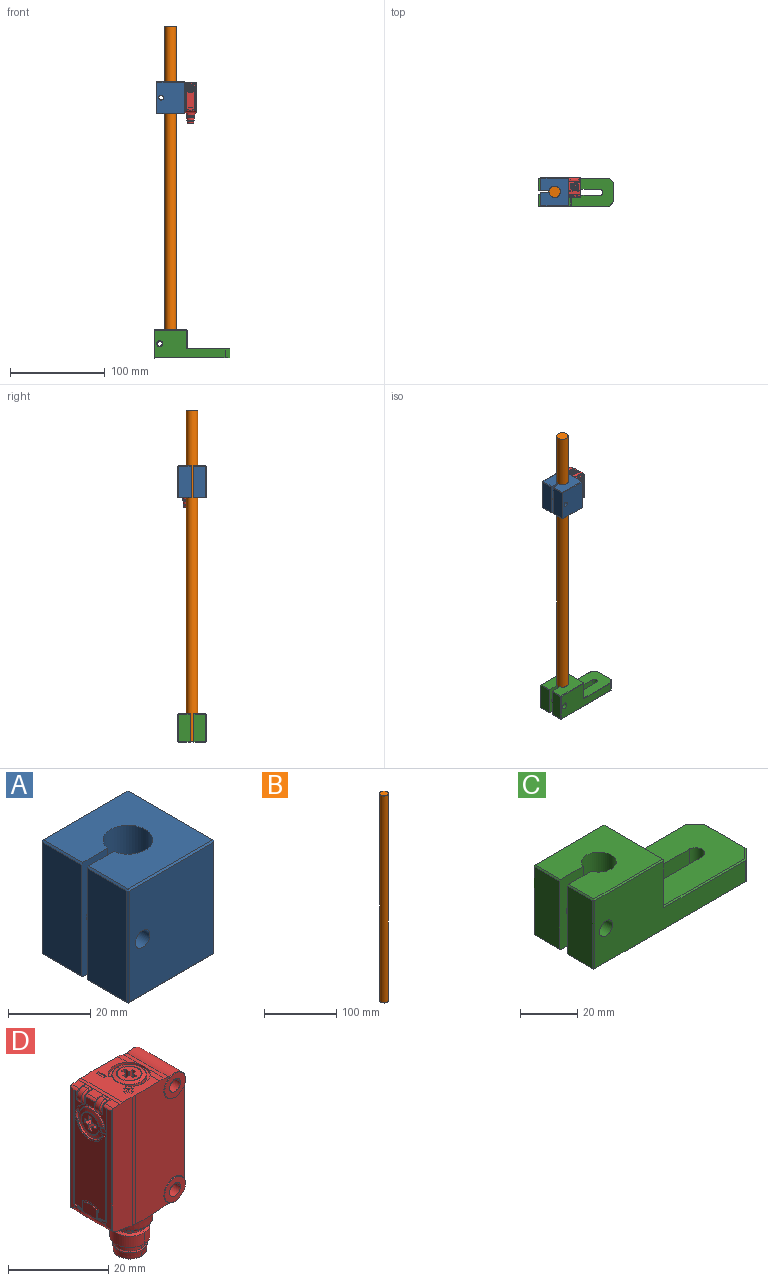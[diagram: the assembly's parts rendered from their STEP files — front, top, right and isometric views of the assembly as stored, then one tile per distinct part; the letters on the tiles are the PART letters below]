
ASSEMBLY  parts=4 mates=3
PART A: 38 faces, bbox 30x30x34 mm
  f0: plane 33x13.5mm, normal (-1,0,0), area 445.5mm2, adj f8,f28,f34,f37
  f1: plane 29x29mm, normal (0,0,1), area 709.1mm2, adj f3,f8,f9,f16,f18,f23,f28,f29
  f2: plane 29x29mm, normal (0,0,-1), area 709.1mm2, adj f3,f8,f9,f20,f25,f31,f35,f37
  f3: cylinder r=6.05mm len=34mm, axis (0,0,1), area 1224.1mm2, adj f1,f2,f8,f9
  f4: plane 33x29mm, normal (1,0,0), area 947.2mm2, adj f11,f13,f23,f24,f30,f31
  f5: plane 33x29mm, normal (0,1,0), area 924.8mm2, adj f15,f18,f19,f24,f25
  f6: plane 33x13.5mm, normal (-1,0,0), area 445.5mm2, adj f9,f16,f19,f20
  f7: plane 33x29mm, normal (0,-1,0), area 937.4mm2, adj f14,f29,f30,f34,f35
  f8: plane 34x9.03mm, normal (0,1,0), area 287.2mm2, adj f0,f1,f2,f3,f14,f28,f37
  f9: plane 34x9.03mm, normal (0,-1,0), area 274.7mm2, adj f1,f2,f3,f6,f15,f16,f20
  f10: cone r=0mm half-angle=59deg, axis (1,0,0), area 5.7mm2, adj f11
  f11: cylinder r=1.25mm len=13.5mm, axis (1,0,0), area 106mm2, adj f4,f10
  f12: cone r=0mm half-angle=59deg, axis (1,0,0), area 5.7mm2, adj f13
  f13: cylinder r=1.25mm len=13.5mm, axis (1,0,0), area 106mm2, adj f4,f12
  f14: cylinder r=2.5mm len=14mm, axis (0,1,0), area 219.9mm2, adj f7,f8
  f15: cylinder r=3.2mm len=14mm, axis (0,-1,0), area 281.5mm2, adj f5,f9
  f16: plane 13.5x0.5mm, normal (-0.71,0,0.71), area 9.5mm2, adj f1,f6,f9,f17
  f17: plane 0.5x0.5mm, normal (-0.58,0.58,0.58), area 0.2mm2, adj f16,f18,f19
  f18: plane 29x0.5mm, normal (0,0.71,0.71), area 20.5mm2, adj f1,f5,f17,f21
  f19: plane 33x0.5mm, normal (-0.71,0.71,0), area 23.3mm2, adj f5,f6,f17,f22
  f20: plane 13.5x0.5mm, normal (-0.71,0,-0.71), area 9.5mm2, adj f2,f6,f9,f22
  f21: plane 0.5x0.5mm, normal (0.58,0.58,0.58), area 0.2mm2, adj f18,f23,f24
  f22: plane 0.5x0.5mm, normal (-0.58,0.58,-0.58), area 0.2mm2, adj f19,f20,f25
  f23: plane 29x0.5mm, normal (0.71,0,0.71), area 20.5mm2, adj f1,f4,f21,f26
  f24: plane 33x0.5mm, normal (0.71,0.71,0), area 23.3mm2, adj f4,f5,f21,f27
  f25: plane 29x0.5mm, normal (0,0.71,-0.71), area 20.5mm2, adj f2,f5,f22,f27
  f26: plane 0.5x0.5mm, normal (0.58,-0.58,0.58), area 0.2mm2, adj f23,f29,f30
  f27: plane 0.5x0.5mm, normal (0.58,0.58,-0.58), area 0.2mm2, adj f24,f25,f31
  f28: plane 13.5x0.5mm, normal (-0.71,0,0.71), area 9.5mm2, adj f0,f1,f8,f32
  f29: plane 29x0.5mm, normal (0,-0.71,0.71), area 20.5mm2, adj f1,f7,f26,f32
  f30: plane 33x0.5mm, normal (0.71,-0.71,0), area 23.3mm2, adj f4,f7,f26,f33
  f31: plane 29x0.5mm, normal (0.71,0,-0.71), area 20.5mm2, adj f2,f4,f27,f33
  f32: plane 0.5x0.5mm, normal (-0.58,-0.58,0.58), area 0.2mm2, adj f28,f29,f34
  f33: plane 0.5x0.5mm, normal (0.58,-0.58,-0.58), area 0.2mm2, adj f30,f31,f35
  f34: plane 33x0.5mm, normal (-0.71,-0.71,0), area 23.3mm2, adj f0,f7,f32,f36
  f35: plane 29x0.5mm, normal (0,-0.71,-0.71), area 20.5mm2, adj f2,f7,f33,f36
  f36: plane 0.5x0.5mm, normal (-0.58,-0.58,-0.58), area 0.2mm2, adj f34,f35,f37
  f37: plane 13.5x0.5mm, normal (-0.71,0,-0.71), area 9.5mm2, adj f0,f2,f8,f36
PART B: 3 faces, bbox 12x12x350 mm
  f0: cylinder r=6mm len=350mm, axis (0,0,-1), area 13194.7mm2, adj f1,f2
  f1: plane 12x12mm, normal (0,0,1), area 113.1mm2, adj f0
  f2: plane 12x12mm, normal (0,0,-1), area 113.1mm2, adj f0
PART C: 53 faces, bbox 80x30x30 mm
  f0: plane 29x12.5mm, normal (-1,0,0), area 362.5mm2, adj f10,f41,f47,f50
  f1: plane 79x29mm, normal (0,0,-1), area 1949.4mm2, adj f2,f10,f11,f14,f15,f16,f17,f20
  f2: cylinder r=6.05mm len=30mm, axis (0,0,1), area 1018.1mm2, adj f1,f3,f10,f11
  f3: plane 34x29mm, normal (0,0,1), area 826.8mm2, adj f2,f10,f11,f18,f25,f32,f41,f42
  f4: plane 29x12.5mm, normal (-1,0,0), area 362.5mm2, adj f11,f18,f19,f20
  f5: plane 19.79x9mm, normal (1,0,0), area 178.1mm2, adj f12,f27,f36,f37
  f6: plane 44.5x29mm, normal (0,0,1), area 1108.2mm2, adj f7,f14,f15,f16,f17,f22,f23,f27
  f7: plane 29x19.5mm, normal (1,0,0), area 565.5mm2, adj f6,f26,f32,f33
  f8: plane 74.29x29mm, normal (0,-1,0), area 1316.5mm2, adj f33,f34,f42,f43,f47,f48,f51
  f9: plane 74.5x29mm, normal (0,1,0), area 1330.9mm2, adj f12,f19,f22,f25,f26,f28,f52
  f10: plane 30x11.79mm, normal (0,1,0), area 321.3mm2, adj f0,f1,f2,f3,f41,f50,f51
  f11: plane 30x11.79mm, normal (0,-1,0), area 333.8mm2, adj f1,f2,f3,f4,f18,f20,f52
  f12: plane 9x5mm, normal (0.71,0.71,0), area 63.6mm2, adj f5,f9,f23,f31
  f13: plane 9x4.71mm, normal (0.71,-0.71,0), area 59.9mm2, adj f35,f36,f43,f44
  f14: cylinder r=3.2mm len=10mm, axis (0,0,1), area 100.5mm2, adj f1,f6,f15,f17
  f15: plane 20x10mm, normal (0,1,0), area 200mm2, adj f1,f6,f14,f16
  f16: cylinder r=3.2mm len=10mm, axis (0,0,1), area 100.5mm2, adj f1,f6,f15,f17
  f17: plane 20x10mm, normal (0,-1,0), area 200mm2, adj f1,f6,f14,f16
  f18: plane 12.5x0.5mm, normal (-0.71,0,0.71), area 8.8mm2, adj f3,f4,f11,f21
  f19: plane 29x0.5mm, normal (-0.71,0.71,0), area 20.5mm2, adj f4,f9,f21,f24
  f20: plane 12.5x0.5mm, normal (-0.71,0,-0.71), area 8.8mm2, adj f1,f4,f11,f24
  f21: plane 0.5x0.5mm, normal (-0.58,0.58,0.58), area 0.2mm2, adj f18,f19,f25
  f22: plane 40.5x0.5mm, normal (0,0.71,0.71), area 28.4mm2, adj f6,f9,f23,f26
  f23: plane 5.21x5.21mm, normal (0.5,0.5,0.71), area 4.9mm2, adj f6,f12,f22,f27
  f24: plane 0.5x0.5mm, normal (-0.58,0.58,-0.58), area 0.2mm2, adj f19,f20,f28
  f25: plane 34x0.5mm, normal (0,0.71,0.71), area 24mm2, adj f3,f9,f21,f29
  f26: plane 20x0.5mm, normal (0.71,0.71,0), area 14mm2, adj f7,f9,f22,f29
  f27: plane 19.79x0.5mm, normal (0.71,0,0.71), area 13.9mm2, adj f5,f6,f23,f30
  f28: plane 74.5x0.5mm, normal (0,0.71,-0.71), area 52.6mm2, adj f1,f9,f24,f31
  f29: plane 0.5x0.5mm, normal (0.58,0.58,0.58), area 0.2mm2, adj f25,f26,f32
  f30: plane 0.5x0.5mm, normal (0.68,-0.28,0.68), area 0.1mm2, adj f27,f35,f36
  f31: plane 5.21x5.21mm, normal (0.5,0.5,-0.71), area 4.9mm2, adj f1,f12,f28,f37
  f32: plane 29x0.5mm, normal (0.71,0,0.71), area 20.5mm2, adj f3,f7,f29,f38
  f33: plane 20x0.5mm, normal (0.71,-0.71,0), area 14mm2, adj f7,f8,f34,f38
  f34: plane 40.29x0.5mm, normal (0,-0.71,0.71), area 28.3mm2, adj f6,f8,f33,f39
  f35: plane 5.06x5.06mm, normal (0.5,-0.5,0.71), area 4.7mm2, adj f6,f13,f30,f39
  f36: plane 9x0.35mm, normal (0.92,-0.38,0), area 3.4mm2, adj f5,f13,f30,f40
  f37: plane 19.79x0.5mm, normal (0.71,0,-0.71), area 13.9mm2, adj f1,f5,f31,f40
  f38: plane 0.5x0.5mm, normal (0.58,-0.58,0.58), area 0.2mm2, adj f32,f33,f42
  f39: plane 0.5x0.5mm, normal (0.28,-0.68,0.68), area 0.1mm2, adj f34,f35,f43
  f40: plane 0.5x0.5mm, normal (0.68,-0.28,-0.68), area 0.1mm2, adj f36,f37,f44
  f41: plane 12.5x0.5mm, normal (-0.71,0,0.71), area 8.8mm2, adj f0,f3,f10,f45
  f42: plane 34x0.5mm, normal (0,-0.71,0.71), area 24mm2, adj f3,f8,f38,f45
  f43: plane 9x0.35mm, normal (0.38,-0.92,0), area 3.4mm2, adj f8,f13,f39,f46
  f44: plane 5.06x5.06mm, normal (0.5,-0.5,-0.71), area 4.7mm2, adj f1,f13,f40,f46
  f45: plane 0.5x0.5mm, normal (-0.58,-0.58,0.58), area 0.2mm2, adj f41,f42,f47
  f46: plane 0.5x0.5mm, normal (0.28,-0.68,-0.68), area 0.1mm2, adj f43,f44,f48
  f47: plane 29x0.5mm, normal (-0.71,-0.71,0), area 20.5mm2, adj f0,f8,f45,f49
  f48: plane 74.29x0.5mm, normal (0,-0.71,-0.71), area 52.5mm2, adj f1,f8,f46,f49
  f49: plane 0.5x0.5mm, normal (-0.58,-0.58,-0.58), area 0.2mm2, adj f47,f48,f50
  f50: plane 12.5x0.5mm, normal (-0.71,0,-0.71), area 8.8mm2, adj f0,f1,f10,f49
  f51: cylinder r=3.2mm len=13mm, axis (0,1,0), area 261.4mm2, adj f8,f10
  f52: cylinder r=2.5mm len=13mm, axis (0,-1,0), area 204.2mm2, adj f9,f11
PART D: 278 faces, bbox 22.2x12.4x43.9 mm
  f0: cylinder r=4.2mm len=8.4mm, axis (0,0,1), area 9.5mm2, adj f1,f3,f4,f21,f22,f23,f24
  f1: plane 8.4x7.8mm, normal (0,0,1), area 14.2mm2, adj f0,f2,f3,f18,f19,f20,f21,f244
  f2: plane 0.6x0.32mm, normal (0.71,0.71,0), area 0.3mm2, adj f1,f3,f4,f18
  f3: cylinder r=4.2mm len=3.42mm, axis (0,0,1), area 2.4mm2, adj f0,f1,f2,f4
  f4: plane 12x10.39mm, normal (0,0,1), area 73.7mm2, adj f0,f2,f3,f5,f6,f7,f8,f9
  f5: plane 0.75x0.3mm, normal (0,1,0), area 0.2mm2, adj f4,f6,f16,f17
  f6: plane 0.7x0.3mm, normal (1,0,0), area 0.2mm2, adj f4,f5,f7,f17
  f7: plane 0.75x0.3mm, normal (0,-1,0), area 0.2mm2, adj f4,f6,f8,f17
  f8: plane 0.75x0.3mm, normal (1,0,0), area 0.2mm2, adj f4,f7,f9,f17
  f9: plane 0.7x0.3mm, normal (0,-1,0), area 0.2mm2, adj f4,f8,f10,f17
  f10: plane 0.75x0.3mm, normal (-1,0,0), area 0.2mm2, adj f4,f9,f11,f17
  f11: plane 0.75x0.3mm, normal (0,-1,0), area 0.2mm2, adj f4,f10,f12,f17
  f12: plane 0.7x0.3mm, normal (-1,0,0), area 0.2mm2, adj f4,f11,f13,f17
  f13: plane 0.75x0.3mm, normal (0,1,0), area 0.2mm2, adj f4,f12,f14,f17
  f14: plane 0.75x0.3mm, normal (-1,0,0), area 0.2mm2, adj f4,f13,f15,f17
  f15: plane 0.7x0.3mm, normal (0,1,0), area 0.2mm2, adj f4,f14,f16,f17
  f16: plane 0.75x0.3mm, normal (1,0,0), area 0.2mm2, adj f4,f5,f15,f17
  f17: plane 2.2x2.2mm, normal (0,0,1), area 2.6mm2, adj f5,f6,f7,f8,f9,f10,f11,f12
  f18: cylinder r=0.2mm len=0.6mm, axis (0,0,1), area 0.2mm2, adj f1,f2,f4,f19
  f19: cylinder r=3.6mm len=3.74mm, axis (0,0,1), area 2.4mm2, adj f1,f4,f18,f20
  f20: cylinder r=0.2mm len=0.6mm, axis (0,0,1), area 0.2mm2, adj f1,f4,f19,f21
  f21: plane 0.6x0.32mm, normal (0.71,-0.71,0), area 0.3mm2, adj f0,f1,f4,f20
  f22: cylinder r=5.84mm len=5.03mm, axis (0,-1,0), area 5.6mm2, adj f0,f4,f23,f62
  f23: plane 11.76x1.31mm, normal (0.25,0,0.97), area 15.1mm2, adj f0,f22,f24,f25,f62,f142
  f24: cylinder r=5.84mm len=5.03mm, axis (0,-1,0), area 5.6mm2, adj f0,f4,f23,f25
  f25: plane 31.53x13.98mm, normal (0.02,1,0), area 377.7mm2, adj f4,f23,f24,f26,f59,f63,f64,f78
  f26: plane 31.38x1mm, normal (0,1,0), area 31.3mm2, adj f4,f25,f27,f59
  f27: plane 31.29x0.05mm, normal (-1,0,0), area 1.6mm2, adj f4,f26,f28,f59
  f28: plane 31.3x5.44mm, normal (-0.02,1,0), area 166.9mm2, adj f4,f27,f29,f40,f41,f45,f56,f59
  f29: cylinder r=1mm len=2.36mm, axis (0,-1,0), area 1.8mm2, adj f28,f30,f39,f40,f55,f56,f57
  f30: plane 28.21x9.39mm, normal (-1,0,0), area 33.7mm2, adj f29,f31,f32,f34,f35,f38,f39,f43
  f31: plane 0.7x0.22mm, normal (0,-0.94,0.35), area 0.2mm2, adj f30,f32,f176,f227
  f32: cylinder r=4.2mm len=8.17mm, axis (1,0,0), area 7.9mm2, adj f30,f31,f33,f34,f166,f172,f176
  f33: plane 3.42x1.97mm, normal (-1,0,0), area 5.1mm2, adj f32,f34,f166,f167,f168,f169
  f34: torus R=1.4mm, axis (0,1,0), area 2.5mm2, adj f30,f32,f33,f35,f169,f170
  f35: cylinder r=1.8mm len=3.22mm, axis (0,-1,0), area 5.4mm2, adj f30,f34,f36,f38
  f36: plane 1.2x0.73mm, normal (0,0,1), area 0.9mm2, adj f35,f37,f170,f171
  f37: cylinder r=0.4mm len=0.88mm, axis (1,0,0), area 0.5mm2, adj f36,f38,f39,f171
  f38: torus R=1.4mm, axis (0,1,0), area 2.5mm2, adj f30,f35,f37,f39
  f39: plane 2.35x2.27mm, normal (0,1,0), area 0.9mm2, adj f29,f30,f37,f38,f40,f171
  f40: plane 11.78x1.75mm, normal (-0.14,0,0.99), area 15.2mm2, adj f28,f29,f39,f41,f42,f43,f159,f164
  f41: cylinder r=4.47mm len=11.81mm, axis (0,-1,0), area 9.3mm2, adj f4,f28,f40,f42
  f42: plane 31.3x5.44mm, normal (-0.02,-1,0), area 166.9mm2, adj f4,f40,f41,f43,f44,f45,f59,f60
  f43: cylinder r=1mm len=2.36mm, axis (0,-1,0), area 1.8mm2, adj f30,f40,f42,f44,f48,f58,f159
  f44: cylinder r=0.2mm len=29.58mm, axis (0,0,1), area 7.8mm2, adj f42,f43,f45,f48
  f45: torus R=76.35mm, axis (-1,0,0), area 29.6mm2, adj f28,f42,f44,f46,f47,f48,f54,f55
  f46: plane 8.39x2.75mm, normal (-1,0,0), area 11.3mm2, adj f45,f47,f49,f50,f51,f52,f53,f54
  f47: cylinder r=0.4mm len=0.64mm, axis (0,0,1), area 0mm2, adj f45,f46,f48,f49
  f48: plane 29.38x1.58mm, normal (-0.97,-0.22,0), area 32.9mm2, adj f43,f44,f45,f47,f49,f58
  f49: plane 2.65x0.47mm, normal (0,0.17,0.98), area 0.5mm2, adj f30,f46,f47,f48,f50,f58
  f50: plane 2.05x0.2mm, normal (0,-1,0), area 0.4mm2, adj f30,f46,f49,f51
  f51: cylinder r=3.7mm len=3.9mm, axis (1,0,0), area 0.8mm2, adj f30,f46,f50,f52
  f52: plane 2.05x0.2mm, normal (0,1,0), area 0.4mm2, adj f30,f46,f51,f53
  f53: plane 2.65x0.47mm, normal (0,-0.17,0.98), area 0.5mm2, adj f30,f46,f52,f54,f55,f57
  f54: cylinder r=0.4mm len=0.64mm, axis (0,0,1), area 0mm2, adj f45,f46,f53,f55
  f55: plane 29.38x1.58mm, normal (-0.97,0.22,0), area 32.9mm2, adj f29,f45,f53,f54,f56,f57
  f56: cylinder r=0.2mm len=29.58mm, axis (0,0,1), area 7.8mm2, adj f28,f29,f45,f55
  f57: plane 27.55x0.12mm, normal (0,-1,0), area 3.2mm2, adj f29,f30,f53,f55
  f58: plane 27.55x0.12mm, normal (0,1,0), area 3.2mm2, adj f30,f43,f48,f49
  f59: torus R=36.05mm, axis (-1,0,0), area 61.3mm2, adj f25,f26,f27,f28,f42,f45,f60,f61
  f60: plane 31.29x0.05mm, normal (-1,0,0), area 1.6mm2, adj f4,f42,f59,f61
  f61: plane 31.38x1mm, normal (0,-1,0), area 31.3mm2, adj f4,f59,f60,f62
  f62: plane 31.53x13.98mm, normal (0.02,-1,0), area 377.7mm2, adj f4,f22,f23,f59,f61,f63,f77,f78
  f63: cylinder r=2.2mm len=11.51mm, axis (0,-1,0), area 7.9mm2, adj f25,f62,f64,f66,f77,f141
  f64: cylinder r=0.1mm len=24.36mm, axis (0,0,1), area 3.7mm2, adj f25,f63,f65,f66,f78
  f65: torus R=75.79mm, axis (-1,0,0), area 1.6mm2, adj f64,f66,f77,f78
  f66: plane 23.72x11.31mm, normal (1,0,0), area 41.3mm2, adj f63,f64,f65,f67,f68,f69,f70,f77
  f67: plane 22.4x1.15mm, normal (0,1,0), area 25.8mm2, adj f66,f68,f70,f71
  f68: plane 10.1x1.15mm, normal (0,0,1), area 11.6mm2, adj f66,f67,f69,f71
  f69: plane 22.4x1.15mm, normal (0,-1,0), area 25.8mm2, adj f66,f68,f70,f71
  f70: plane 10.1x1.15mm, normal (0,0,-1), area 11.6mm2, adj f66,f67,f69,f71
  f71: plane 22.4x10.1mm, normal (1,0,0), area 6.5mm2, adj f67,f68,f69,f70,f72,f73,f74,f75
  f72: plane 9.9x1.1mm, normal (0,0,-1), area 10.9mm2, adj f71,f73,f75,f76
  f73: plane 22.2x1.1mm, normal (0,-1,0), area 24.4mm2, adj f71,f72,f74,f76
  f74: plane 9.9x1.1mm, normal (0,0,1), area 10.9mm2, adj f71,f73,f75,f76
  f75: plane 22.2x1.1mm, normal (0,1,0), area 24.4mm2, adj f71,f72,f74,f76
  f76: plane 22.2x9.9mm, normal (1,0,0), area 219.8mm2, adj f72,f73,f74,f75
  f77: cylinder r=0.1mm len=24.36mm, axis (0,0,1), area 3.7mm2, adj f62,f63,f65,f66,f78
  f78: cylinder r=3mm len=11.8mm, axis (0,-1,0), area 3.5mm2, adj f25,f62,f64,f65,f77,f79,f81,f95
  f79: cylinder r=3mm len=11.8mm, axis (0,-1,0), area 71.3mm2, adj f25,f62,f78,f80,f94,f96
  f80: torus R=2.9mm, axis (0,1,0), area 1.5mm2, adj f79,f81,f82
  f81: torus R=2.9mm, axis (0,1,0), area 1.5mm2, adj f78,f80,f82
  f82: plane 5.8x5.8mm, normal (0,1,0), area 19.1mm2, adj f80,f81,f83,f84
  f83: cylinder r=1.53mm len=3.06mm, axis (0,-1,0), area 9.6mm2, adj f82,f84,f86
  f84: cylinder r=1.53mm len=3.06mm, axis (0,-1,0), area 9.6mm2, adj f82,f83,f85
  f85: cone r=1.23mm half-angle=45deg, axis (0,1,0), area 1.8mm2, adj f84,f86,f88
  f86: cone r=1.23mm half-angle=45deg, axis (0,1,0), area 1.8mm2, adj f83,f85,f87
  f87: cylinder r=1.23mm len=7.4mm, axis (0,-1,0), area 28.6mm2, adj f86,f88,f90
  f88: cylinder r=1.23mm len=7.4mm, axis (0,-1,0), area 28.6mm2, adj f85,f87,f89
  f89: cone r=1.53mm half-angle=45deg, axis (0,-1,0), area 1.8mm2, adj f88,f90,f92
  f90: cone r=1.53mm half-angle=45deg, axis (0,-1,0), area 1.8mm2, adj f87,f89,f91
  f91: cylinder r=1.53mm len=3.06mm, axis (0,-1,0), area 9.6mm2, adj f90,f92,f93
  f92: cylinder r=1.53mm len=3.06mm, axis (0,-1,0), area 9.6mm2, adj f89,f91,f93
  f93: plane 5.8x5.8mm, normal (0,-1,0), area 19.1mm2, adj f91,f92,f94,f95
  f94: torus R=2.9mm, axis (0,1,0), area 1.5mm2, adj f79,f93,f95
  f95: torus R=2.9mm, axis (0,1,0), area 1.5mm2, adj f78,f93,f94
  f96: torus R=36.05mm, axis (-1,0,0), area 20.4mm2, adj f25,f62,f79,f97,f101
  f97: plane 12.3x8.55mm, normal (0,0,-1), area 21.1mm2, adj f25,f59,f62,f96,f98,f101
  f98: cone r=4.95mm half-angle=6deg, axis (0,0,1), area 50.9mm2, adj f97,f99,f100,f101
  f99: torus R=4mm, axis (0,0,-1), area 10.8mm2, adj f98,f100,f101,f102
  f100: torus R=4mm, axis (0,0,-1), area 10.8mm2, adj f98,f99,f101,f102
  f101: cone r=4.95mm half-angle=6deg, axis (0,0,1), area 50.9mm2, adj f96,f97,f98,f99,f100
  f102: plane 8.01x8.01mm, normal (0,0,-1), area 14mm2, adj f99,f100,f103,f104
  f103: cylinder r=3.4mm len=6.8mm, axis (0,0,1), area 10.7mm2, adj f102,f104,f106
  f104: cylinder r=3.4mm len=6.8mm, axis (0,0,1), area 10.7mm2, adj f102,f103,f105
  f105: cone r=3.4mm half-angle=60deg, axis (0,0,-1), area 8.1mm2, adj f104,f106,f108
  f106: cone r=3.4mm half-angle=60deg, axis (0,0,-1), area 8.1mm2, adj f103,f105,f107
  f107: cylinder r=4mm len=8mm, axis (0,0,1), area 34.2mm2, adj f106,f108,f110
  f108: cylinder r=4mm len=8mm, axis (0,0,1), area 34.2mm2, adj f105,f107,f109
  f109: cone r=4mm half-angle=60deg, axis (0,0,1), area 9.9mm2, adj f108,f110,f112
  f110: cone r=4mm half-angle=60deg, axis (0,0,1), area 9.9mm2, adj f107,f109,f111
  f111: cylinder r=3.25mm len=6.5mm, axis (0,0,1), area 10.2mm2, adj f110,f112,f114
  f112: cylinder r=3.25mm len=6.5mm, axis (0,0,1), area 10.2mm2, adj f109,f111,f113
  f113: cone r=3.25mm half-angle=38.7deg, axis (0,0,-1), area 2.9mm2, adj f112,f114,f116
  f114: cone r=3.25mm half-angle=38.7deg, axis (0,0,-1), area 2.9mm2, adj f111,f113,f115
  f115: torus R=3.35mm, axis (0,0,-1), area 0.9mm2, adj f114,f116,f118
  f116: torus R=3.35mm, axis (0,0,-1), area 0.9mm2, adj f113,f115,f117
  f117: cone r=3.45mm half-angle=6.5deg, axis (0,0,1), area 16.3mm2, adj f116,f118,f120
  f118: cone r=3.45mm half-angle=6.5deg, axis (0,0,1), area 16.3mm2, adj f115,f117,f119
  f119: torus R=3.07mm, axis (0,0,-1), area 2.9mm2, adj f118,f120,f121
  f120: torus R=3.07mm, axis (0,0,-1), area 2.9mm2, adj f117,f119,f121
  f121: plane 6.14x6.14mm, normal (0,0,-1), area 3.2mm2, adj f119,f120,f122,f123
  f122: cylinder r=2.9mm len=5.8mm, axis (0,0,1), area 45.6mm2, adj f121,f123,f124
  f123: cylinder r=2.9mm len=5.8mm, axis (0,0,1), area 45.6mm2, adj f121,f122,f124
  f124: plane 5.8x5.8mm, normal (0,0,-1), area 23.3mm2, adj f122,f123,f125,f126,f129,f130,f133,f134
  f125: cylinder r=0.5mm len=4.2mm, axis (0,0,1), area 6.6mm2, adj f124,f126,f128
  f126: cylinder r=0.5mm len=4.2mm, axis (0,0,1), area 6.6mm2, adj f124,f125,f127
  f127: sphere r=0.5mm, area 0.9mm2, adj f126,f128
  f128: sphere r=0.5mm, area 0.9mm2, adj f125,f127
  f129: cylinder r=0.5mm len=4.2mm, axis (0,0,1), area 6.6mm2, adj f124,f130,f132
  f130: cylinder r=0.5mm len=4.2mm, axis (0,0,1), area 6.6mm2, adj f124,f129,f131
  f131: sphere r=0.5mm, area 0.9mm2, adj f130,f132
  f132: sphere r=0.5mm, area 0.9mm2, adj f129,f131
  f133: cylinder r=0.5mm len=4.2mm, axis (0,0,1), area 6.6mm2, adj f124,f134,f136
  f134: cylinder r=0.5mm len=4.2mm, axis (0,0,1), area 6.6mm2, adj f124,f133,f135
  f135: sphere r=0.5mm, area 0.9mm2, adj f134,f136
  f136: sphere r=0.5mm, area 0.9mm2, adj f133,f135
  f137: cylinder r=0.5mm len=4.2mm, axis (0,0,1), area 6.6mm2, adj f124,f138,f140
  f138: cylinder r=0.5mm len=4.2mm, axis (0,0,1), area 6.6mm2, adj f124,f137,f139
  f139: sphere r=0.5mm, area 0.9mm2, adj f138,f140
  f140: sphere r=0.5mm, area 0.9mm2, adj f137,f139
  f141: cylinder r=3mm len=11.8mm, axis (0,-1,0), area 11.1mm2, adj f25,f62,f63,f142,f144,f157
  f142: cylinder r=3mm len=11.8mm, axis (0,-1,0), area 74.6mm2, adj f23,f25,f62,f141,f143,f158
  f143: torus R=2.9mm, axis (0,1,0), area 1.5mm2, adj f142,f144,f145
  f144: torus R=2.9mm, axis (0,1,0), area 1.5mm2, adj f141,f143,f145
  f145: plane 5.8x5.8mm, normal (0,-1,0), area 19.1mm2, adj f143,f144,f146,f147
  f146: cylinder r=1.53mm len=3.06mm, axis (0,-1,0), area 9.6mm2, adj f145,f147,f149
  f147: cylinder r=1.53mm len=3.06mm, axis (0,-1,0), area 9.6mm2, adj f145,f146,f148
  f148: cone r=1.53mm half-angle=45deg, axis (0,-1,0), area 1.8mm2, adj f147,f149,f151
  f149: cone r=1.53mm half-angle=45deg, axis (0,-1,0), area 1.8mm2, adj f146,f148,f150
  f150: cylinder r=1.23mm len=7.4mm, axis (0,-1,0), area 28.6mm2, adj f149,f151,f153
  f151: cylinder r=1.23mm len=7.4mm, axis (0,-1,0), area 28.6mm2, adj f148,f150,f152
  f152: cone r=1.23mm half-angle=45deg, axis (0,1,0), area 1.8mm2, adj f151,f153,f155
  f153: cone r=1.23mm half-angle=45deg, axis (0,1,0), area 1.8mm2, adj f150,f152,f154
  f154: cylinder r=1.53mm len=3.06mm, axis (0,-1,0), area 9.6mm2, adj f153,f155,f156
  f155: cylinder r=1.53mm len=3.06mm, axis (0,-1,0), area 9.6mm2, adj f152,f154,f156
  f156: plane 5.8x5.8mm, normal (0,1,0), area 19.1mm2, adj f154,f155,f157,f158
  f157: torus R=2.9mm, axis (0,1,0), area 1.5mm2, adj f141,f156,f158
  f158: torus R=2.9mm, axis (0,1,0), area 1.5mm2, adj f142,f156,f157
  f159: plane 2.35x2.27mm, normal (0,-1,0), area 0.9mm2, adj f30,f40,f43,f160,f163,f164
  f160: torus R=1.4mm, axis (0,1,0), area 2.5mm2, adj f30,f159,f161,f163
  f161: cylinder r=1.8mm len=3.22mm, axis (0,-1,0), area 5.4mm2, adj f30,f160,f162,f166
  f162: plane 1.2x0.73mm, normal (0,0,1), area 0.9mm2, adj f161,f163,f164,f165
  f163: cylinder r=0.4mm len=0.88mm, axis (1,0,0), area 0.5mm2, adj f159,f160,f162,f164
  f164: plane 2.06x0.66mm, normal (0.94,0,0.34), area 1.2mm2, adj f40,f159,f162,f163,f165,f167
  f165: cylinder r=0.4mm len=0.88mm, axis (1,0,0), area 0.5mm2, adj f162,f164,f166,f167
  f166: torus R=1.4mm, axis (0,1,0), area 2.5mm2, adj f30,f32,f33,f161,f165,f167
  f167: plane 2.35x2.27mm, normal (0,1,0), area 0.9mm2, adj f33,f40,f164,f165,f166,f168
  f168: cylinder r=1mm len=3mm, axis (0,-1,0), area 2.3mm2, adj f33,f40,f167,f169
  f169: plane 2.35x2.27mm, normal (0,-1,0), area 0.9mm2, adj f33,f34,f40,f168,f170,f171
  f170: cylinder r=0.4mm len=0.88mm, axis (1,0,0), area 0.5mm2, adj f34,f36,f169,f171
  f171: plane 2.06x0.66mm, normal (0.94,0,0.34), area 1.2mm2, adj f36,f37,f39,f40,f169,f170
  f172: plane 0.7x0.22mm, normal (0,0.94,0.35), area 0.2mm2, adj f30,f32,f173,f176
  f173: cylinder r=0.17mm len=0.7mm, axis (1,0,0), area 0.1mm2, adj f30,f172,f174,f176
  f174: plane 0.7x0.18mm, normal (0,0.77,-0.64), area 0.2mm2, adj f30,f173,f175,f176
  f175: cylinder r=4.2mm len=1.11mm, axis (1,0,0), area 0.8mm2, adj f30,f174,f176,f222
  f176: plane 8.4x7.85mm, normal (-1,0,0), area 10.2mm2, adj f31,f32,f172,f173,f174,f175,f177,f178
  f177: cone r=3.46mm half-angle=5deg, axis (1,0,0), area 5mm2, adj f176,f178,f181,f212
  f178: cone r=3.46mm half-angle=5deg, axis (1,0,0), area 5mm2, adj f176,f177,f179,f180
  f179: plane 1.59x0.82mm, normal (0,0,-1), area 0.4mm2, adj f176,f178,f180,f183,f184,f186,f213,f214
  f180: torus R=3.36mm, axis (1,0,0), area 1.2mm2, adj f178,f179,f181,f183
  f181: torus R=3.36mm, axis (1,0,0), area 1.2mm2, adj f177,f180,f182,f212
  f182: cone r=2.56mm half-angle=75deg, axis (1,0,0), area 7.5mm2, adj f181,f183,f185,f212
  f183: cone r=2.56mm half-angle=75deg, axis (1,0,0), area 7.5mm2, adj f179,f180,f182,f184
  f184: torus R=2.43mm, axis (1,0,0), area 1mm2, adj f179,f183,f185,f186
  f185: torus R=2.43mm, axis (1,0,0), area 1mm2, adj f182,f184,f186,f212
  f186: plane 5.47x4.87mm, normal (-1,0,0), area 13.7mm2, adj f179,f184,f185,f187,f188,f190,f191,f192
  f187: plane 1.9x0.75mm, normal (0,1,0), area 1.4mm2, adj f186,f188,f189,f211
  f188: cylinder r=0.1mm len=1.9mm, axis (1,0,0), area 0.3mm2, adj f186,f187,f189,f190
  f189: plane 3.4x3.4mm, normal (-1,0,0), area 5.6mm2, adj f187,f188,f190,f191,f192,f193,f194,f195
  f190: plane 1.9x0.93mm, normal (0,0,1), area 1.8mm2, adj f186,f188,f189,f191
  f191: cylinder r=0.2mm len=1.9mm, axis (1,0,0), area 0.6mm2, adj f186,f189,f190,f192
  f192: plane 1.9x0.93mm, normal (0,1,0), area 1.8mm2, adj f186,f189,f191,f193
  f193: cylinder r=0.1mm len=1.9mm, axis (1,0,0), area 0.3mm2, adj f186,f189,f192,f194
  f194: plane 1.9x0.75mm, normal (0,0,1), area 1.4mm2, adj f186,f189,f193,f195
  f195: cylinder r=0.1mm len=1.9mm, axis (1,0,0), area 0.3mm2, adj f186,f189,f194,f196
  f196: plane 1.9x0.93mm, normal (0,-1,0), area 1.8mm2, adj f186,f189,f195,f197
  f197: cylinder r=0.2mm len=1.9mm, axis (1,0,0), area 0.6mm2, adj f186,f189,f196,f198
  f198: plane 1.9x0.93mm, normal (0,0,1), area 1.8mm2, adj f186,f189,f197,f199
  f199: cylinder r=0.1mm len=1.9mm, axis (1,0,0), area 0.3mm2, adj f186,f189,f198,f200
  f200: plane 1.9x0.75mm, normal (0,-1,0), area 1.4mm2, adj f186,f189,f199,f201
  f201: cylinder r=0.1mm len=1.9mm, axis (1,0,0), area 0.3mm2, adj f186,f189,f200,f202
  f202: plane 1.9x0.93mm, normal (0,0,-1), area 1.8mm2, adj f186,f189,f201,f203
  f203: cylinder r=0.2mm len=1.9mm, axis (1,0,0), area 0.6mm2, adj f186,f189,f202,f204
  f204: plane 1.9x0.93mm, normal (0,-1,0), area 1.8mm2, adj f186,f189,f203,f205
  f205: cylinder r=0.1mm len=1.9mm, axis (1,0,0), area 0.3mm2, adj f186,f189,f204,f206
  f206: plane 1.9x0.75mm, normal (0,0,-1), area 1.4mm2, adj f186,f189,f205,f207
  f207: cylinder r=0.1mm len=1.9mm, axis (1,0,0), area 0.3mm2, adj f186,f189,f206,f208
  f208: plane 1.9x0.93mm, normal (0,1,0), area 1.8mm2, adj f186,f189,f207,f209
  f209: cylinder r=0.2mm len=1.9mm, axis (1,0,0), area 0.6mm2, adj f186,f189,f208,f210
  f210: plane 1.9x0.93mm, normal (0,0,-1), area 1.8mm2, adj f186,f189,f209,f211
  f211: cylinder r=0.1mm len=1.9mm, axis (1,0,0), area 0.3mm2, adj f186,f187,f189,f210
  f212: plane 1.59x0.82mm, normal (0,0,1), area 0.4mm2, adj f176,f177,f181,f182,f185,f186,f213,f214
  f213: cylinder r=0.5mm len=1.09mm, axis (0,0,1), area 0.1mm2, adj f179,f186,f212,f214
  f214: plane 1.09x0.92mm, normal (-0.97,-0.26,0), area 1mm2, adj f179,f212,f213,f215,f216,f217,f218,f219
  f215: plane 0.58x0.14mm, normal (0,-0.62,0.79), area 0.1mm2, adj f176,f212,f214,f216
  f216: cylinder r=4.1mm len=0.54mm, axis (1,0,0), area 0mm2, adj f176,f214,f215,f217
  f217: plane 0.81x0.54mm, normal (0,-1,0), area 0.4mm2, adj f176,f214,f216,f218
  f218: cylinder r=4.1mm len=0.54mm, axis (1,0,0), area 0mm2, adj f176,f214,f217,f219
  f219: plane 0.58x0.14mm, normal (0,-0.62,-0.79), area 0.1mm2, adj f176,f179,f214,f218
  f220: cylinder r=3.65mm len=7.13mm, axis (1,0,0), area 6.9mm2, adj f30,f176,f221,f223
  f221: cylinder r=0.1mm len=0.7mm, axis (1,0,0), area 0.1mm2, adj f30,f176,f220,f222
  f222: plane 0.7x0.48mm, normal (0,0,1), area 0.3mm2, adj f30,f175,f176,f221
  f223: cylinder r=0.1mm len=0.7mm, axis (1,0,0), area 0.1mm2, adj f30,f176,f220,f224
  f224: plane 0.7x0.48mm, normal (0,0,1), area 0.3mm2, adj f30,f176,f223,f225
  f225: cylinder r=4.2mm len=1.11mm, axis (1,0,0), area 0.8mm2, adj f30,f176,f224,f226
  f226: plane 0.7x0.18mm, normal (0,-0.77,-0.64), area 0.2mm2, adj f30,f176,f225,f227
  f227: cylinder r=0.17mm len=0.7mm, axis (1,0,0), area 0.1mm2, adj f30,f31,f176,f226
  f228: cylinder r=3.95mm len=7.53mm, axis (-1,0,0), area 1mm2, adj f30,f229,f236,f238
  f229: plane 20.67x8.6mm, normal (-1,0,0), area 150.9mm2, adj f228,f230,f231,f232,f233,f234,f235,f236
  f230: cylinder r=19.7mm len=2.05mm, axis (-1,0,0), area 0.2mm2, adj f30,f229,f231,f237
  f231: plane 1.98x0.1mm, normal (0,1,0), area 0.2mm2, adj f30,f229,f230,f232
  f232: cylinder r=4mm len=4.5mm, axis (-1,0,0), area 0.5mm2, adj f30,f229,f231,f233
  f233: plane 1.98x0.1mm, normal (0,-1,0), area 0.2mm2, adj f30,f229,f232,f234
  f234: cylinder r=19.7mm len=2.05mm, axis (-1,0,0), area 0.2mm2, adj f30,f229,f233,f235
  f235: plane 20.32x0.1mm, normal (0,1,0), area 2mm2, adj f30,f229,f234,f236
  f236: plane 0.54x0.1mm, normal (0,0,1), area 0.1mm2, adj f30,f228,f229,f235
  f237: plane 20.32x0.1mm, normal (0,-1,0), area 2mm2, adj f30,f229,f230,f238
  f238: plane 0.54x0.1mm, normal (0,0,1), area 0.1mm2, adj f30,f228,f229,f237
  f239: plane 2.2x0.3mm, normal (1,0,0), area 0.7mm2, adj f4,f240,f242,f243
  f240: plane 0.7x0.3mm, normal (0,-1,0), area 0.2mm2, adj f4,f239,f241,f243
  f241: plane 2.2x0.3mm, normal (-1,0,0), area 0.7mm2, adj f4,f240,f242,f243
  f242: plane 0.7x0.3mm, normal (0,1,0), area 0.2mm2, adj f4,f239,f241,f243
  f243: plane 2.2x0.7mm, normal (0,0,1), area 1.5mm2, adj f239,f240,f241,f242
  f244: cone r=3.45mm half-angle=5deg, axis (0,0,-1), area 5.2mm2, adj f1,f245,f247
  f245: cone r=3.45mm half-angle=5deg, axis (0,0,-1), area 5.2mm2, adj f1,f244,f246
  f246: torus R=3.35mm, axis (0,0,-1), area 1.3mm2, adj f245,f247,f249
  f247: torus R=3.35mm, axis (0,0,-1), area 1.3mm2, adj f244,f246,f248
  f248: cone r=2.56mm half-angle=75deg, axis (0,0,-1), area 7.9mm2, adj f247,f249,f251
  f249: cone r=2.56mm half-angle=75deg, axis (0,0,-1), area 7.9mm2, adj f246,f248,f250
  f250: torus R=2.43mm, axis (0,0,-1), area 1mm2, adj f249,f251,f252
  f251: torus R=2.43mm, axis (0,0,-1), area 1mm2, adj f248,f250,f252
  f252: plane 4.87x4.87mm, normal (0,0,1), area 13.6mm2, adj f250,f251,f253,f254,f255,f257,f258,f259
  f253: cylinder r=0.2mm len=2mm, axis (0,0,-1), area 0.6mm2, adj f252,f254,f256,f277
  f254: plane 2x0.61mm, normal (0,1,0), area 1.2mm2, adj f252,f253,f255,f256
  f255: cylinder r=0.1mm len=2mm, axis (0,0,-1), area 0.3mm2, adj f252,f254,f256,f258
  f256: plane 3.4x2.77mm, normal (0,0,1), area 5mm2, adj f253,f254,f255,f257,f258,f259,f260,f261
  f257: cylinder r=0.1mm len=2mm, axis (0,0,-1), area 0.3mm2, adj f252,f256,f258,f259
  f258: plane 2x0.75mm, normal (1,0,0), area 1.5mm2, adj f252,f255,f256,f257
  f259: plane 2x0.61mm, normal (0,-1,0), area 1.2mm2, adj f252,f256,f257,f260
  f260: cylinder r=0.2mm len=2mm, axis (0,0,-1), area 0.6mm2, adj f252,f256,f259,f261
  f261: plane 2x0.93mm, normal (1,0,0), area 1.8mm2, adj f252,f256,f260,f262
  f262: cylinder r=0.1mm len=2mm, axis (0,0,-1), area 0.3mm2, adj f252,f256,f261,f263
  f263: plane 2x0.75mm, normal (0,-1,0), area 1.5mm2, adj f252,f256,f262,f264
  f264: cylinder r=0.1mm len=2mm, axis (0,0,-1), area 0.3mm2, adj f252,f256,f263,f265
  f265: plane 2x0.93mm, normal (-1,0,0), area 1.8mm2, adj f252,f256,f264,f266
  f266: cylinder r=0.2mm len=2mm, axis (0,0,-1), area 0.6mm2, adj f252,f256,f265,f267
  f267: plane 2x0.61mm, normal (0,-1,0), area 1.2mm2, adj f252,f256,f266,f268
  f268: cylinder r=0.1mm len=2mm, axis (0,0,-1), area 0.3mm2, adj f252,f256,f267,f269
  f269: plane 2x0.75mm, normal (-1,0,0), area 1.5mm2, adj f252,f256,f268,f270
  f270: cylinder r=0.1mm len=2mm, axis (0,0,-1), area 0.3mm2, adj f252,f256,f269,f271
  f271: plane 2x0.61mm, normal (0,1,0), area 1.2mm2, adj f252,f256,f270,f272
  f272: cylinder r=0.2mm len=2mm, axis (0,0,-1), area 0.6mm2, adj f252,f256,f271,f273
  f273: plane 2x0.93mm, normal (-1,0,0), area 1.8mm2, adj f252,f256,f272,f274
  f274: cylinder r=0.1mm len=2mm, axis (0,0,-1), area 0.3mm2, adj f252,f256,f273,f275
  f275: plane 2x0.75mm, normal (0,1,0), area 1.5mm2, adj f252,f256,f274,f276
  f276: cylinder r=0.1mm len=2mm, axis (0,0,-1), area 0.3mm2, adj f252,f256,f275,f277
  f277: plane 2x0.93mm, normal (1,0,0), area 1.8mm2, adj f252,f253,f256,f276
PLACE A t=(-20.98,1.69,-53.19)mm
PLACE B t=(-20.98,1.69,-152.63)mm
PLACE C t=(1.52,1.69,-312.63)mm fixed
PLACE D rot(axis=(0,0,1),91deg) t=(-0.05,7.1,-68.89)mm
MATE slider D.f25 <-> A.f12  axis (-1,0,0) through (-5.98,13.69,-40.49)mm
MATE slider A.f3 <-> B.f0  axis (0,0,1) through (-20.98,1.69,-36.19)mm
MATE slider B.f0 <-> C.f2  axis (0,0,-1) through (-20.98,1.69,-327.63)mm
